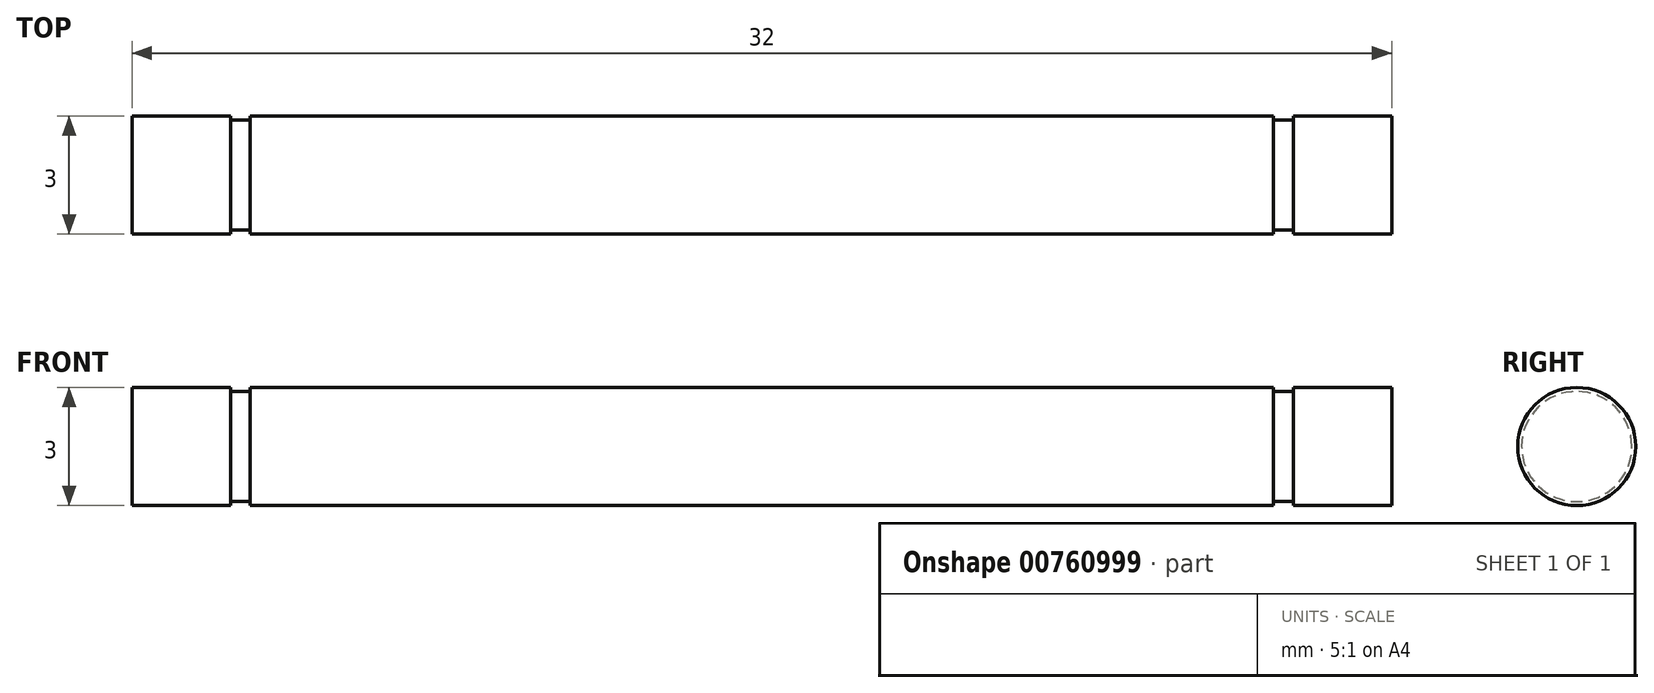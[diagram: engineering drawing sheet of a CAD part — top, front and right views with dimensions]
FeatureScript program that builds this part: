
annotation { "Feature Type Name" : "Feature", "Feature Type Description" : "" }
export const myFeature = defineFeature(function(context is Context, id is Id, definition is map)
    precondition{}
    {
        {
            var Q0;
            Q0=qCreatedBy(makeId("Right.planeOp"),FACE);
            var sketch = newSketch(context, id + "F0", { "sketchPlane" : qUnion([Q0])});
            skCircle(sketch, "E0", {"center": v(0, 0) * mm, "radius": 1.5 * mm});
            skSolve(sketch);
        }
        {
            var Q0;
            Q0 = qSketchRegion(id + "F0", true);
            extrude(context, id + "F1", {"entities" : qUnion([Q0]), "depth" : 26 * mm, "offsetDistance" : 25 * mm});
        }
        {
            var Q0;
            Q0=makeQuery(id+"F1.opExtrude","CAP_FACE",FACE,{"disambiguationData":[OSD([sQuery(id+"F0.wireOp",EDGE,"E0")])],"isStart":false});
            var sketch = newSketch(context, id + "F2", { "sketchPlane" : qUnion([Q0])});
            skCircle(sketch, "E1", {"center": v(0, 0) * mm, "radius": 1.4 * mm});
            skSolve(sketch);
        }
        {
            var Q0;
            Q0 = qSketchRegion(id + "F2", true);
            extrude(context, id + "F3", {"entities" : qUnion([Q0]), "operationType" : NewBodyOperationType.ADD, "depth" : 0.5 * mm, "offsetDistance" : 25 * mm});
        }
        {
            var Q0;
            Q0=makeQuery(id+"F1.opExtrude","CAP_FACE",FACE,{"disambiguationData":[OSD([sQuery(id+"F0.wireOp",EDGE,"E0")])],"isStart":true});
            var sketch = newSketch(context, id + "F4", { "sketchPlane" : qUnion([Q0])});
            skCircle(sketch, "E2", {"center": v(0, 0) * mm, "radius": 1.4 * mm});
            skSolve(sketch);
        }
        {
            var Q0;
            Q0 = qSketchRegion(id + "F4", true);
            extrude(context, id + "F5", {"entities" : qUnion([Q0]), "operationType" : NewBodyOperationType.ADD, "depth" : 0.5 * mm, "offsetDistance" : 25 * mm});
        }
        {
            var Q0;
            Q0=makeQuery(id+"F5.opExtrude","CAP_FACE",FACE,{"disambiguationData":[OSD([sQuery(id+"F4.wireOp",EDGE,"E2")])],"isStart":false});
            var sketch = newSketch(context, id + "F6", { "sketchPlane" : qUnion([Q0])});
            skCircle(sketch, "E3", {"center": v(0, 0) * mm, "radius": 1.5 * mm});
            skSolve(sketch);
        }
        {
            var Q0;
            Q0 = qSketchRegion(id + "F6", true);
            extrude(context, id + "F7", {"entities" : qUnion([Q0]), "operationType" : NewBodyOperationType.ADD, "depth" : 2.5 * mm, "offsetDistance" : 25 * mm});
        }
        {
            var Q0;
            Q0=makeQuery(id+"F3.opExtrude","CAP_FACE",FACE,{"disambiguationData":[OSD([sQuery(id+"F2.wireOp",EDGE,"E1")])],"isStart":false});
            var sketch = newSketch(context, id + "F8", { "sketchPlane" : qUnion([Q0])});
            skCircle(sketch, "E4", {"center": v(0, 0) * mm, "radius": 1.5 * mm});
            skSolve(sketch);
        }
        {
            var Q0;
            Q0 = qSketchRegion(id + "F8", true);
            extrude(context, id + "F9", {"entities" : qUnion([Q0]), "operationType" : NewBodyOperationType.ADD, "depth" : 2.5 * mm, "offsetDistance" : 25 * mm});
        }
    });
